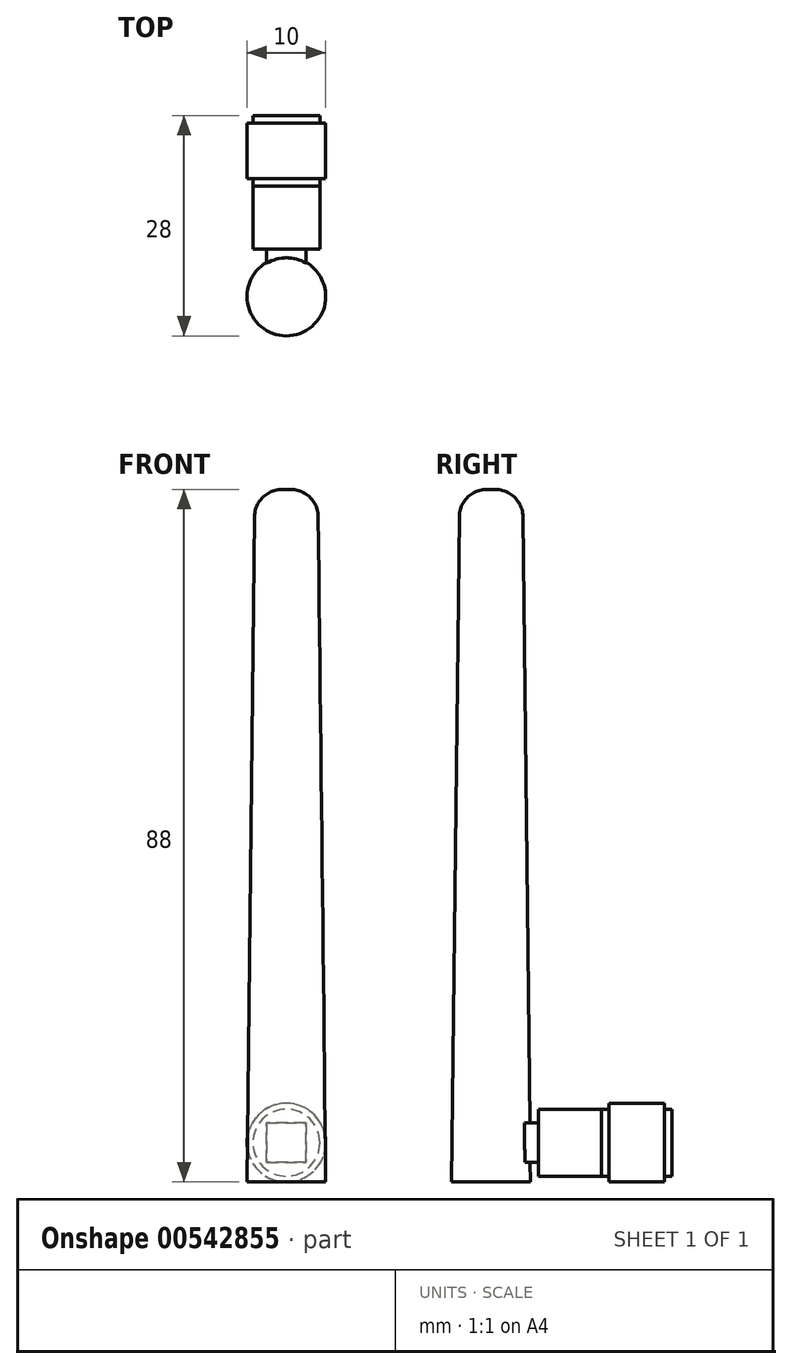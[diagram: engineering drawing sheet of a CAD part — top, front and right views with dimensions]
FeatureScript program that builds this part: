
annotation { "Feature Type Name" : "Feature", "Feature Type Description" : "" }
export const myFeature = defineFeature(function(context is Context, id is Id, definition is map)
    precondition{}
    {
        {
            var Q0;
            Q0=qCreatedBy(makeId("Front.planeOp"),FACE);
            var sketch = newSketch(context, id + "F0", { "sketchPlane" : qUnion([Q0])});
            skCircle(sketch, "E0", {"center": v(0, 0) * mm, "radius": 4.25 * mm});
            skSolve(sketch);
        }
        {
            var Q0;
            Q0 = qSketchRegion(id + "F0", true);
            extrude(context, id + "F1", {"entities" : qUnion([Q0]), "depth" : 1 * mm, "offsetDistance" : 25 * mm});
        }
        {
            var Q0;
            Q0=makeQuery(id+"F1.opExtrude","CAP_FACE",FACE,{"disambiguationData":[OSD([sQuery(id+"F0.wireOp",EDGE,"E0")])],"isStart":false});
            var sketch = newSketch(context, id + "F2", { "sketchPlane" : qUnion([Q0])});
            skCircle(sketch, "E1", {"center": v(0, 0) * mm, "radius": 5 * mm});
            skSolve(sketch);
        }
        {
            var Q0;
            Q0 = qSketchRegion(id + "F2", true);
            extrude(context, id + "F3", {"entities" : qUnion([Q0]), "operationType" : NewBodyOperationType.ADD, "depth" : 7 * mm, "offsetDistance" : 25 * mm});
        }
        {
            var Q0;
            Q0=makeQuery(id+"F3.opExtrude","CAP_FACE",FACE,{"disambiguationData":[OSD([sQuery(id+"F2.wireOp",EDGE,"E1")])],"isStart":false});
            var sketch = newSketch(context, id + "F4", { "sketchPlane" : qUnion([Q0])});
            skCircle(sketch, "E2", {"center": v(0, 0) * mm, "radius": 4.25 * mm});
            skSolve(sketch);
        }
        {
            var Q0;
            Q0 = qSketchRegion(id + "F4", true);
            extrude(context, id + "F5", {"entities" : qUnion([Q0]), "operationType" : NewBodyOperationType.ADD, "depth" : 1 * mm, "offsetDistance" : 25 * mm});
        }
        {
            var Q0;
            Q0=makeQuery(id+"F5.opExtrude","CAP_FACE",FACE,{"disambiguationData":[OSD([sQuery(id+"F4.wireOp",EDGE,"E2")])],"isStart":false});
            extrude(context, id + "F6", {"entities" : qUnion([Q0]), "depth" : 8 * mm, "offsetDistance" : 25 * mm});
        }
        {
            var Q0;
            Q0=makeQuery(id+"F6.opExtrude","CAP_FACE",FACE,{"disambiguationData":[OSD([sQuery(id+"F4.wireOp",EDGE,"E2")])],"isStart":false});
            var sketch = newSketch(context, id + "F7", { "sketchPlane" : qUnion([Q0])});
            skLineSegment(sketch, "E3.bottom", {"start": v(2.5, -2.5) * mm, "end": v(-2.5, -2.5) * mm});
            skLineSegment(sketch, "E3.top", {"start": v(2.5, 2.5) * mm, "end": v(-2.5, 2.5) * mm});
            skLineSegment(sketch, "E3.left", {"start": v(2.5, -2.5) * mm, "end": v(2.5, 2.5) * mm});
            skLineSegment(sketch, "E3.right", {"start": v(-2.5, -2.5) * mm, "end": v(-2.5, 2.5) * mm});
            skPoint(sketch, "E3.middle", {"position": v(0, 0) * mm});
            skSolve(sketch);
        }
        {
            var Q0;
            Q0=makeQuery(id+"F7.imprint","IMPRINT",FACE,{"disambiguationData":[TD([[makeQuery(id+"F7.imprint","IMPRINT",EDGE,{"derivedFrom":sQuery(id+"F7.wireOp",EDGE,"E3.bottom")}),-1.0]])]});
            extrude(context, id + "F8", {"entities" : qUnion([Q0]), "operationType" : NewBodyOperationType.ADD, "depth" : 7 * mm, "offsetDistance" : 25 * mm});
        }
        {
            var Q0;
            Q0=makeQuery(id+"F8.opExtrude","CAP_EDGE",EDGE,{"disambiguationData":[OSD([sQuery(id+"F7.wireOp",EDGE,"E3.top")])],"isStart":false});
            var Q1;
            Q1=makeQuery(id+"F8.opExtrude","CAP_EDGE",EDGE,{"disambiguationData":[OSD([sQuery(id+"F7.wireOp",EDGE,"E3.bottom")])],"isStart":false});
            fillet(context, id + "F9", {"entities" : qUnion([Q0, Q1]), "radius" : 2.5 * mm, "tangentPropagation" : true, "allowEdgeOverflow" : false});
        }
        {
            var Q0;
            Q0=qCreatedBy(makeId("Top.planeOp"),FACE);
            cPlane(context, id + "F10", {"entities" : qUnion([Q0]), "cplaneType" : CPlaneType.OFFSET, "offset" : 5 * mm, "oppositeDirection" : true, "width" : 150 * mm, "height" : 150 * mm});
        }
        {
            var Q0;
            Q0=qCreatedBy(id+"F10.planeOp",FACE);
            var sketch = newSketch(context, id + "F11", { "sketchPlane" : qUnion([Q0])});
            skCircle(sketch, "E4", {"center": v(0, -23) * mm, "radius": 5 * mm});
            skLineSegment(sketch, "E5", {"start": v(0, -23) * mm, "end": v(0, 0) * mm, "construction": true});
            skSolve(sketch);
        }
        {
            var Q0;
            Q0=qCreatedBy(id+"F10.planeOp",FACE);
            cPlane(context, id + "F12", {"entities" : qUnion([Q0]), "cplaneType" : CPlaneType.OFFSET, "offset" : 88 * mm, "width" : 150 * mm, "height" : 150 * mm});
        }
        {
            var Q0;
            Q0=qCreatedBy(id+"F12.planeOp",FACE);
            var sketch = newSketch(context, id + "F13", { "sketchPlane" : qUnion([Q0])});
            skCircle(sketch, "E6", {"center": v(0, -23) * mm, "radius": 4 * mm});
            skSolve(sketch);
        }
        {
            var Q1;
            Q1 = qSketchRegion(id + "F11", true);
            var Q2;
            Q2 = qSketchRegion(id + "F13", true);
            loft(context, id + "F14", {"operationType" : NewBodyOperationType.ADD, "sheetProfilesArray" : [{ "sheetProfileEntities" : qUnion([Q1]) }, { "sheetProfileEntities" : qUnion([Q2]) }]});
        }
        {
            var Q0;
            Q0=makeQuery(id+"F14.opLoft","MID_CAP_EDGE",EDGE,{"disambiguationData":[OSD([sQuery(id+"F11.wireOp",EDGE,"E4"),sQuery(id+"F13.wireOp",EDGE,"E6")])],"capPos":1.0});
            fillet(context, id + "F15", {"entities" : qUnion([Q0]), "radius" : 3.5 * mm, "tangentPropagation" : true, "allowEdgeOverflow" : false});
        }
    });
